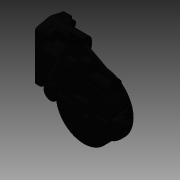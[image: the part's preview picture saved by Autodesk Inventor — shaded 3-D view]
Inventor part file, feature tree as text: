
AUTODESK INVENTOR PART (.ipt)
format: ipt  version: 2014 SP1 (Build 180222100, 222)  size: 222,208 bytes
history: native  units: in
note: dims shown in document units (in); Inventor stores cm internally (conversion verified against a paired STEP export)
features: fillet x1, other x1, imported_body x1
ambient origin geometry x8: Origin, YZ Plane, XZ Plane, XY Plane, X Axis, Y Axis, Z Axis, Center Point
bodies: Body1 (feature_tree)
feature tree (3):
  fillet  "Fillet1"  [1 undecoded]
  other  "AM-2235 gearbox housing1"
  imported_body  "Base1"
note: 1 required parameter value undecoded (feature->parameter linkage not recoverable at this tier; creation-order binding heuristic only, values carry confidence <= 0.55)
